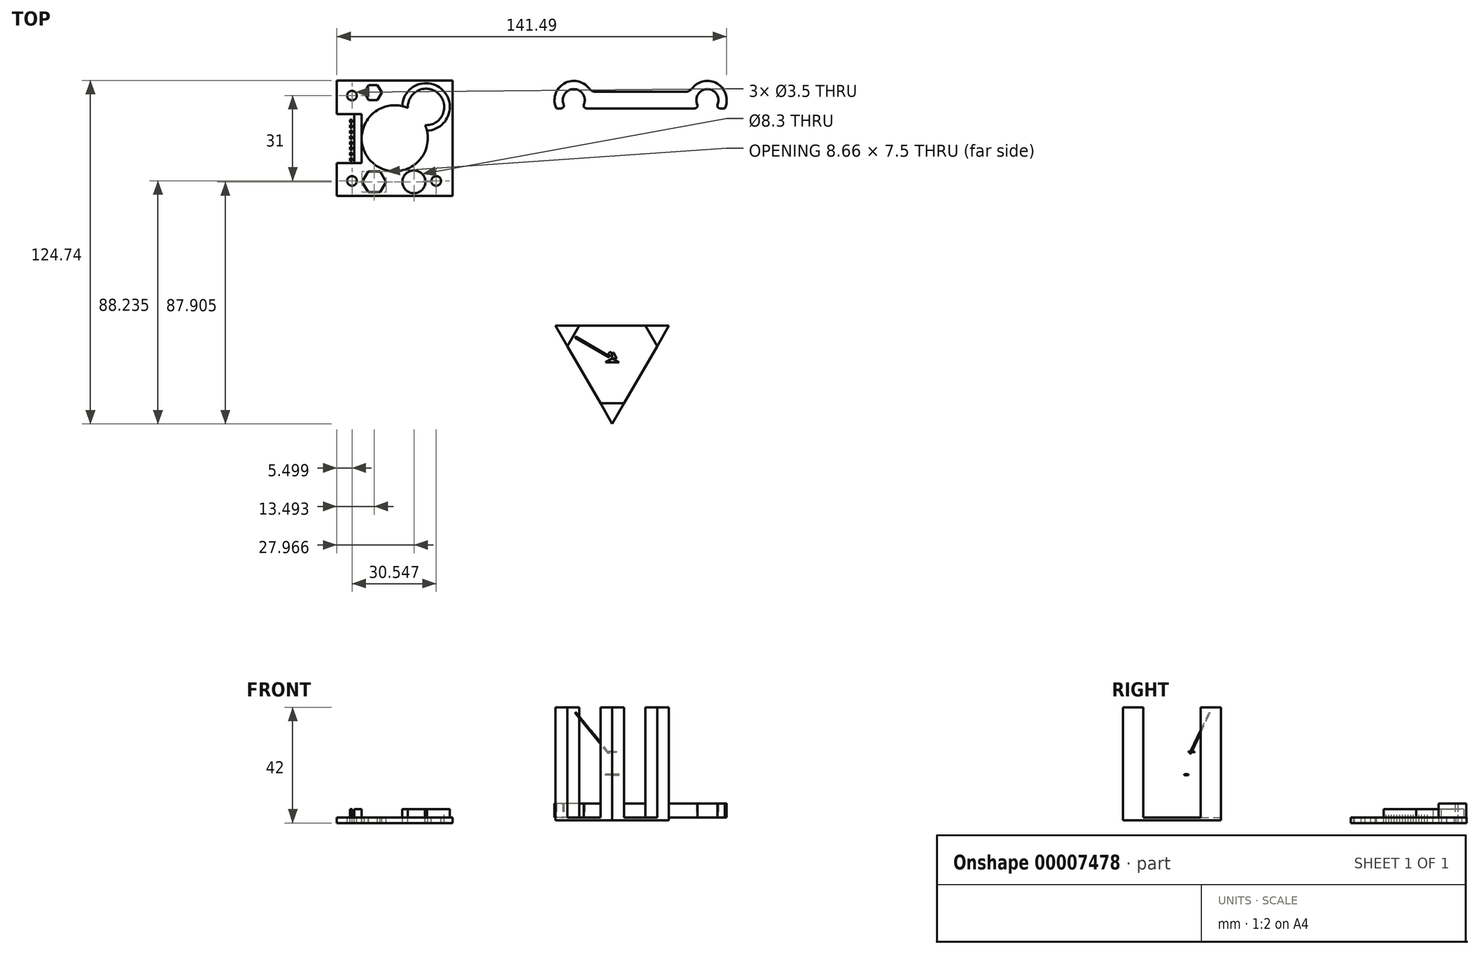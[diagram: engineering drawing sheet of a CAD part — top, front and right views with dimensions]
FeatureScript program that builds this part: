
annotation { "Feature Type Name" : "Feature", "Feature Type Description" : "" }
export const myFeature = defineFeature(function(context is Context, id is Id, definition is map)
    precondition{}
    {
        {
            var Q0;
            Q0=qCreatedBy(makeId("Top.planeOp"),FACE);
            var sketch = newSketch(context, id + "F0", { "sketchPlane" : qUnion([Q0])});
            skLineSegment(sketch, "E0.rect.bottom", {"start": v(36, -3) * mm, "end": v(-19.67, -3) * mm});
            skLineSegment(sketch, "E0.rect.top", {"start": v(36, 3) * mm, "end": v(-16.25, 3) * mm});
            skLineSegment(sketch, "E0.rect.left", {"start": v(36, -3) * mm, "end": v(36, 3) * mm});
            skPoint(sketch, "E0.rect.middle", {"position": v(0, 0) * mm});
            skArc(sketch, "E1", {"start": v(-18.65, 4.2) * mm, "mid": v(-27.87, 6) * mm, "end": v(-30.57, -3) * mm});
            skArc(sketch, "E2", {"start": v(-20.58, -1.6) * mm, "mid": v(-24.25, 4) * mm, "end": v(-27.92, -1.6) * mm});
            skLineSegment(sketch, "E3", {"start": v(-28.83, -3) * mm, "end": v(-30.57, -3) * mm});
            skPoint(sketch, "E0.rect.right.end.orphan", {"position": v(-36, 3) * mm});
            skLineSegment(sketch, "E4", {"start": v(0, 3) * mm, "end": v(0, -3) * mm});
            skPoint(sketch, "E5.orphan", {"position": v(-36, -3) * mm});
            skPoint(sketch, "E6.visualSharp", {"position": v(-26.9, -3) * mm});
            skArc(sketch, "E6.filletArc", {"start": v(-28.83, -3) * mm, "mid": v(-28, -2.55) * mm, "end": v(-27.92, -1.6) * mm});
            skPoint(sketch, "E7.visualSharp", {"position": v(-21.6, -3) * mm});
            skArc(sketch, "E7.filletArc", {"start": v(-20.58, -1.6) * mm, "mid": v(-20.5, -2.55) * mm, "end": v(-19.67, -3) * mm});
            skArc(sketch, "E8.filletArc", {"start": v(-18.65, 4.2) * mm, "mid": v(-17.6, 3.32) * mm, "end": v(-16.25, 3) * mm});
            skSolve(sketch);
        }
        {
            var Q0;
            Q0=makeQuery(id+"F0.imprint","IMPRINT",FACE,{"disambiguationData":[TD([[makeQuery(id+"F0.imprint","IMPRINT",EDGE,{"derivedFrom":sQuery(id+"F0.wireOp",EDGE,"E1")}),1.0]])]});
            extrude(context, id + "F1", {"entities" : qUnion([Q0]), "depth" : 5 * mm});
        }
        {
            var Q0;
            Q0=makeQuery(id+"F1.opExtrude","SWEPT_BODY",BODY,{"disambiguationData":[OSD([sQuery(id+"F0.wireOp",EDGE,"E0.rect.bottom"),sQuery(id+"F0.wireOp",EDGE,"E0.rect.top"),sQuery(id+"F0.wireOp",EDGE,"E1"),sQuery(id+"F0.wireOp",EDGE,"E2"),sQuery(id+"F0.wireOp",EDGE,"E3"),sQuery(id+"F0.wireOp",EDGE,"E4"),sQuery(id+"F0.wireOp",EDGE,"E6.filletArc"),sQuery(id+"F0.wireOp",EDGE,"E7.filletArc"),sQuery(id+"F0.wireOp",EDGE,"E8.filletArc")])]});
            var Q1;
            Q1=makeQuery(id+"F1.opExtrude","SWEPT_FACE",FACE,{"disambiguationData":[OSD([sQuery(id+"F0.wireOp",EDGE,"E4")])]});
            mirror(context, id + "F2", {"operationType" : NewBodyOperationType.ADD, "entities" : qUnion([Q0]), "mirrorPlane" : qUnion([Q1])});
        }
        {
            var Q0;
            Q0=qCreatedBy(makeId("Top.planeOp"),FACE);
            var sketch = newSketch(context, id + "F3", { "sketchPlane" : qUnion([Q0])});
            skCircle(sketch, "E9.cCircle", {"center": v(-10.28, -93.84) * mm, "radius": 11.87 * mm, "construction": true});
            skLineSegment(sketch, "E9.0", {"start": v(-30.84, -81.97) * mm, "end": v(10.29, -81.97) * mm});
            skLineSegment(sketch, "E9.1", {"start": v(10.29, -81.97) * mm, "end": v(-10.28, -117.59) * mm});
            skLineSegment(sketch, "E9.2", {"start": v(-10.28, -117.59) * mm, "end": v(-30.84, -81.97) * mm});
            skPoint(sketch, "E9.0.midPoint", {"position": v(-10.28, -81.97) * mm});
            skLineSegment(sketch, "E10", {"start": v(-22.28, -81.97) * mm, "end": v(-26.56, -89.39) * mm});
            skLineSegment(sketch, "E11.1.0", {"start": v(-14.56, -110.17) * mm, "end": v(-6, -110.17) * mm});
            skLineSegment(sketch, "E11.2.0", {"start": v(6, -89.39) * mm, "end": v(1.72, -81.97) * mm});
            skSolve(sketch);
        }
        {
            var Q0;
            {var subQ0=sQuery(id+"F3.wireOp",EDGE,"E10");Q0=makeQuery(id+"F3.imprint","IMPRINT",FACE,{"disambiguationData":[TD([[makeQuery(id+"F3.imprint","IMPRINT",EDGE,{"derivedFrom":subQ0}),-1.0]])]});}
            var Q1;
            {var subQ0=sQuery(id+"F3.wireOp",EDGE,"E11.1.0");Q1=makeQuery(id+"F3.imprint","IMPRINT",FACE,{"disambiguationData":[TD([[makeQuery(id+"F3.imprint","IMPRINT",EDGE,{"derivedFrom":subQ0}),-1.0]])]});}
            var Q2;
            {var subQ0=sQuery(id+"F3.wireOp",EDGE,"E11.2.0");Q2=makeQuery(id+"F3.imprint","IMPRINT",FACE,{"disambiguationData":[TD([[makeQuery(id+"F3.imprint","IMPRINT",EDGE,{"derivedFrom":subQ0}),-1.0]])]});}
            var Q3;
            {var subQ2=sQuery(id+"F3.wireOp",EDGE,"E10");Q3=makeQuery(id+"F3.imprint","IMPRINT",FACE,{"disambiguationData":[TD([[makeQuery(id+"F3.imprint","IMPRINT",EDGE,{"derivedFrom":subQ2}),1.0]])]});}
            extrude(context, id + "F4", {"entities" : qUnion([Q0, Q1, Q2, Q3]), "oppositeDirection" : true, "depth" : 1 * mm});
        }
        {
            var Q0;
            {var subQ0=sQuery(id+"F3.wireOp",EDGE,"E10");Q0=makeQuery(id+"F3.imprint","IMPRINT",FACE,{"disambiguationData":[TD([[makeQuery(id+"F3.imprint","IMPRINT",EDGE,{"derivedFrom":subQ0}),-1.0]])]});}
            var Q1;
            {var subQ0=sQuery(id+"F3.wireOp",EDGE,"E11.1.0");Q1=makeQuery(id+"F3.imprint","IMPRINT",FACE,{"disambiguationData":[TD([[makeQuery(id+"F3.imprint","IMPRINT",EDGE,{"derivedFrom":subQ0}),-1.0]])]});}
            var Q2;
            {var subQ0=sQuery(id+"F3.wireOp",EDGE,"E11.2.0");Q2=makeQuery(id+"F3.imprint","IMPRINT",FACE,{"disambiguationData":[TD([[makeQuery(id+"F3.imprint","IMPRINT",EDGE,{"derivedFrom":subQ0}),-1.0]])]});}
            extrude(context, id + "F5", {"entities" : qUnion([Q0, Q1, Q2]), "operationType" : NewBodyOperationType.ADD, "depth" : 40 * mm});
        }
        {
            var Q0;
            {var subQ2=sQuery(id+"F3.wireOp",EDGE,"E10");Q0=makeQuery(id+"F3.imprint","IMPRINT",FACE,{"disambiguationData":[TD([[makeQuery(id+"F3.imprint","IMPRINT",EDGE,{"derivedFrom":subQ2}),1.0]])]});}
            cPlane(context, id + "F6", {"entities" : qUnion([Q0]), "cplaneType" : CPlaneType.OFFSET, "offset" : 24 * mm, "width" : 150 * mm, "height" : 150 * mm});
        }
        {
            var Q0;
            Q0=qCreatedBy(id+"F6.planeOp",FACE);
            var sketch = newSketch(context, id + "F7", { "sketchPlane" : qUnion([Q0])});
            skLineSegment(sketch, "E12", {"start": v(-11.53, -93.12) * mm, "end": v(-24.42, -85.68) * mm});
            skLineSegment(sketch, "E13.0", {"start": v(-22.28, -81.97) * mm, "end": v(-26.56, -89.39) * mm});
            skPoint(sketch, "E14.0", {"position": v(-10.28, -93.84) * mm});
            skLineSegment(sketch, "E15", {"start": v(-10.28, -93.84) * mm, "end": v(-12.78, -95.29) * mm});
            skLineSegment(sketch, "E16", {"start": v(-12.78, -95.29) * mm, "end": v(-10.28, -90.96) * mm});
            skLineSegment(sketch, "E17", {"start": v(-10.28, -90.96) * mm, "end": v(-10.28, -93.84) * mm});
            skLineSegment(sketch, "E18", {"start": v(-10.28, -93.84) * mm, "end": v(-6.88, -93.84) * mm});
            skLineSegment(sketch, "E19", {"start": v(-11, -92.21) * mm, "end": v(-12.05, -94.03) * mm});
            skLineSegment(sketch, "E20.1.0", {"start": v(-7.78, -95.29) * mm, "end": v(-12.78, -95.29) * mm});
            skLineSegment(sketch, "E20.1.1", {"start": v(-12.78, -95.29) * mm, "end": v(-10.28, -93.84) * mm});
            skLineSegment(sketch, "E20.1.2", {"start": v(-10.28, -93.84) * mm, "end": v(-7.78, -95.29) * mm});
            skLineSegment(sketch, "E20.2.0", {"start": v(-10.28, -90.96) * mm, "end": v(-7.78, -95.29) * mm});
            skLineSegment(sketch, "E20.2.1", {"start": v(-7.78, -95.29) * mm, "end": v(-10.28, -93.84) * mm});
            skLineSegment(sketch, "E20.2.2", {"start": v(-10.28, -93.84) * mm, "end": v(-10.28, -90.96) * mm});
            skLineSegment(sketch, "E21", {"start": v(-11, -92.21) * mm, "end": v(-9.55, -92.21) * mm});
            skCircle(sketch, "E22", {"center": v(-11, -92.21) * mm, "radius": 0.6 * mm});
            skCircle(sketch, "E23", {"center": v(-9.55, -92.21) * mm, "radius": 0.6 * mm});
            skSolve(sketch);
        }
        {
            var Q0;
            Q0=sQuery(id+"F7.wireOp",EDGE,"E12");
            var Q1;
            Q1=makeQuery(id+"F5.opExtrude","CAP_FACE",FACE,{"disambiguationData":[OSD([sQuery(id+"F3.wireOp",EDGE,"E9.0"),sQuery(id+"F3.wireOp",EDGE,"E9.2"),sQuery(id+"F3.wireOp",EDGE,"E10")])],"isStart":false});
            extrude(context, id + "F8", {"bodyType" : ToolBodyType.SURFACE, "surfaceEntities" : qUnion([Q0]), "endBound" : BoundingType.UP_TO_SURFACE, "endBoundEntityFace" : qUnion([Q1]), "depth" : 25 * mm});
        }
        {
            var Q0;
            Q0=makeQuery(id+"F8.opExtrude","SWEPT_FACE",FACE,{"disambiguationData":[OSD([sQuery(id+"F7.wireOp",EDGE,"E12")])]});
            var sketch = newSketch(context, id + "F9", { "sketchPlane" : qUnion([Q0])});
            skLineSegment(sketch, "E24", {"start": v(-22.7, 38) * mm, "end": v(-36.58, 23.33) * mm});
            skLineSegment(sketch, "E25", {"start": v(-36.58, 23.33) * mm, "end": v(-22.7, 23.33) * mm});
            skLineSegment(sketch, "E26", {"start": v(-22.7, 23.33) * mm, "end": v(-22.7, 38) * mm});
            skLineSegment(sketch, "E27", {"start": v(-22.7, 38) * mm, "end": v(-21.7, 38) * mm});
            skLineSegment(sketch, "E28", {"start": v(-22.7, 38) * mm, "end": v(-24.45, 17.88) * mm});
            skLineSegment(sketch, "E29", {"start": v(-24.45, 17.88) * mm, "end": v(-22.7, 17.88) * mm});
            skLineSegment(sketch, "E30", {"start": v(-22.7, 17.88) * mm, "end": v(-22.7, 23.33) * mm});
            skPoint(sketch, "E31.0", {"position": v(-21.7, 0) * mm});
            skCircle(sketch, "E32", {"center": v(-22.7, 38) * mm, "radius": 20.2 * mm, "construction": true});
            skLineSegment(sketch, "E33.0", {"start": v(-22.84, 38.14) * mm, "end": v(-36.72, 23.47) * mm});
            skLineSegment(sketch, "E34", {"start": v(-36.72, 23.47) * mm, "end": v(-36.58, 23.33) * mm});
            skLineSegment(sketch, "E35", {"start": v(-22.7, 38) * mm, "end": v(-22.84, 38.14) * mm});
            skLineSegment(sketch, "E36", {"start": v(-36.58, 23.33) * mm, "end": v(-36.58, 19.83) * mm});
            skLineSegment(sketch, "E37", {"start": v(-24.45, 17.88) * mm, "end": v(-24.45, 14.38) * mm});
            skLineSegment(sketch, "E38.0", {"start": v(-42.47, 40) * mm, "end": v(-42.47, 0) * mm});
            skSolve(sketch);
        }
        {
            var Q0;
            {var subQ0=sQuery(id+"F7.wireOp",EDGE,"E22");var subQ3=sQuery(id+"F7.wireOp",EDGE,"E16");var subQ4=makeQuery(id+"F7.imprint","INTERSECT",VERTEX,{"derivedFrom":[subQ3,subQ0]});Q0=makeQuery(id+"F7.imprint","IMPRINT",FACE,{"disambiguationData":[TD([[makeQuery(id+"F7.imprint","IMPRINT",EDGE,{"disambiguationData":[TD([[subQ4,1.0]])],"derivedFrom":subQ0}),1.0]])]});}
            var Q1;
            {var subQ0=sQuery(id+"F7.wireOp",EDGE,"E22");var subQ3=sQuery(id+"F7.wireOp",EDGE,"E19");var subQ4=makeQuery(id+"F7.imprint","INTERSECT",VERTEX,{"derivedFrom":[subQ3,subQ0]});Q1=makeQuery(id+"F7.imprint","IMPRINT",FACE,{"disambiguationData":[TD([[makeQuery(id+"F7.imprint","IMPRINT",EDGE,{"disambiguationData":[TD([[subQ4,-1.0]])],"derivedFrom":subQ0}),1.0]])]});}
            var Q2;
            {var subQ3=sQuery(id+"F7.wireOp",EDGE,"E20.1.1");Q2=makeQuery(id+"F7.imprint","IMPRINT",FACE,{"disambiguationData":[TD([[makeQuery(id+"F7.imprint","IMPRINT",EDGE,{"derivedFrom":subQ3}),1.0]])]});}
            var Q3;
            {var subQ1=sQuery(id+"F7.wireOp",EDGE,"E21");var subQ5=sQuery(id+"F7.wireOp",EDGE,"E20.2.2");var subQ6=makeQuery(id+"F7.imprint","INTERSECT",VERTEX,{"derivedFrom":[subQ5,subQ1]});Q3=makeQuery(id+"F7.imprint","IMPRINT",FACE,{"disambiguationData":[TD([[makeQuery(id+"F7.imprint","IMPRINT",EDGE,{"disambiguationData":[TD([[subQ6,1.0]])],"derivedFrom":subQ1}),1.0]])]});}
            var Q4;
            {var subQ1=sQuery(id+"F7.wireOp",EDGE,"E21");var subQ5=sQuery(id+"F7.wireOp",EDGE,"E20.2.2");var subQ6=makeQuery(id+"F7.imprint","INTERSECT",VERTEX,{"derivedFrom":[subQ5,subQ1]});Q4=makeQuery(id+"F7.imprint","IMPRINT",FACE,{"disambiguationData":[TD([[makeQuery(id+"F7.imprint","IMPRINT",EDGE,{"disambiguationData":[TD([[subQ6,-1.0]])],"derivedFrom":subQ1}),1.0]])]});}
            var Q5;
            {var subQ1=sQuery(id+"F7.wireOp",EDGE,"E21");var subQ3=sQuery(id+"F7.wireOp",EDGE,"E20.2.0");var subQ5=makeQuery(id+"F7.imprint","INTERSECT",VERTEX,{"derivedFrom":[subQ3,subQ1]});Q5=makeQuery(id+"F7.imprint","IMPRINT",FACE,{"disambiguationData":[TD([[makeQuery(id+"F7.imprint","IMPRINT",EDGE,{"disambiguationData":[TD([[subQ5,1.0]])],"derivedFrom":subQ3}),-1.0]])]});}
            var Q6;
            {var subQ1=sQuery(id+"F7.wireOp",EDGE,"E21");var subQ3=sQuery(id+"F7.wireOp",EDGE,"E20.2.0");var subQ5=makeQuery(id+"F7.imprint","INTERSECT",VERTEX,{"derivedFrom":[subQ3,subQ1]});Q6=makeQuery(id+"F7.imprint","IMPRINT",FACE,{"disambiguationData":[TD([[makeQuery(id+"F7.imprint","IMPRINT",EDGE,{"disambiguationData":[TD([[subQ5,-1.0]])],"derivedFrom":subQ3}),-1.0]])]});}
            var Q7;
            {var subQ3=sQuery(id+"F7.wireOp",EDGE,"E20.2.0");var subQ7=sQuery(id+"F7.wireOp",EDGE,"E18");var subQ9=makeQuery(id+"F7.imprint","INTERSECT",VERTEX,{"derivedFrom":[subQ7,subQ3]});Q7=makeQuery(id+"F7.imprint","IMPRINT",FACE,{"disambiguationData":[TD([[makeQuery(id+"F7.imprint","IMPRINT",EDGE,{"disambiguationData":[TD([[subQ9,1.0]])],"derivedFrom":subQ3}),-1.0]])]});}
            var Q8;
            {var subQ0=sQuery(id+"F7.wireOp",EDGE,"E20.2.1");Q8=makeQuery(id+"F7.imprint","IMPRINT",FACE,{"disambiguationData":[TD([[makeQuery(id+"F7.imprint","IMPRINT",EDGE,{"derivedFrom":subQ0}),-1.0]])]});}
            var Q9;
            Q9=makeQuery(id+"F7.imprint","IMPRINT",FACE,{"disambiguationData":[TD([[makeQuery(id+"F7.imprint","IMPRINT",EDGE,{"derivedFrom":sQuery(id+"F7.wireOp",EDGE,"E20.1.0")}),-1.0]])]});
            extrude(context, id + "F10", {"entities" : qUnion([Q0, Q1, Q2, Q3, Q4, Q5, Q6, Q7, Q8, Q9]), "oppositeDirection" : true, "depth" : 0.3 * mm});
        }
        {
            var Q0;
            Q0=makeQuery(id+"F10.opExtrude","SWEPT_BODY",BODY,{"disambiguationData":[OSD([sQuery(id+"F7.wireOp",EDGE,"E16"),sQuery(id+"F7.wireOp",EDGE,"E19"),sQuery(id+"F7.wireOp",EDGE,"E20.1.0"),sQuery(id+"F7.wireOp",EDGE,"E20.2.0")])]});
            var Q1;
            Q1=sQuery(id+"F9.wireOp",EDGE,"E26");
            transform(context, id + "F11", {"entities" : qUnion([Q0]), "transformType" : TransformType.TRANSLATION_3D, "dx" : 0 * mm, "dy" : 0 * mm, "dz" : -8.29 * mm, "makeCopy" : false});
        }
        {
            var Q0;
            {var subQ5=sQuery(id+"F9.wireOp",EDGE,"E35");Q0=makeQuery(id+"F9.imprint","IMPRINT",FACE,{"disambiguationData":[TD([[makeQuery(id+"F9.imprint","IMPRINT",EDGE,{"derivedFrom":subQ5}),1.0]])]});}
            var Q1;
            {var subQ0=sQuery(id+"F9.wireOp",EDGE,"E34");Q1=makeQuery(id+"F9.imprint","IMPRINT",FACE,{"disambiguationData":[TD([[makeQuery(id+"F9.imprint","IMPRINT",EDGE,{"derivedFrom":subQ0}),1.0]])]});}
            var Q2;
            Q2=sQuery(id+"F9.wireOp",EDGE,"E24");
            revolve(context, id + "F12", {"entities" : qUnion([Q0, Q1]), "axis" : qUnion([Q2]), "revolveType" : RevolveType.FULL});
        }
        {
            var Q0;
            Q0=qCreatedBy(makeId("Top.planeOp"),FACE);
            var sketch = newSketch(context, id + "F13", { "sketchPlane" : qUnion([Q0])});
            skLineSegment(sketch, "E39.rect.bottom", {"start": v(-68.24, -34.85) * mm, "end": v(-110.24, -34.85) * mm});
            skLineSegment(sketch, "E39.rect.top", {"start": v(-68.24, 7.15) * mm, "end": v(-110.24, 7.15) * mm});
            skLineSegment(sketch, "E39.rect.left", {"start": v(-68.24, -34.85) * mm, "end": v(-68.24, 7.15) * mm});
            skLineSegment(sketch, "E39.rect.right", {"start": v(-110.24, -34.85) * mm, "end": v(-110.24, 7.15) * mm});
            skPoint(sketch, "E39.rect.middle", {"position": v(-89.24, -13.85) * mm});
            skCircle(sketch, "E40", {"center": v(-77.87, -2.49) * mm, "radius": 6.62 * mm});
            skLineSegment(sketch, "E41", {"start": v(-77.87, -2.49) * mm, "end": v(-68.24, 7.15) * mm});
            skCircle(sketch, "E42", {"center": v(-89.24, -13.85) * mm, "radius": 12 * mm});
            skLineSegment(sketch, "E43.0", {"start": v(-68.24, -29.35) * mm, "end": v(-104.74, -29.35) * mm, "construction": true});
            skLineSegment(sketch, "E43.1", {"start": v(-104.74, -29.35) * mm, "end": v(-104.74, 1.65) * mm, "construction": true});
            skLineSegment(sketch, "E43.2", {"start": v(-68.24, 1.65) * mm, "end": v(-104.74, 1.65) * mm, "construction": true});
            skCircle(sketch, "E44", {"center": v(-104.74, 1.65) * mm, "radius": 1.75 * mm});
            skCircle(sketch, "E45", {"center": v(-104.74, -29.35) * mm, "radius": 1.75 * mm});
            skCircle(sketch, "E46", {"center": v(-74.2, -29.35) * mm, "radius": 1.75 * mm});
            skLineSegment(sketch, "E47.bottom", {"start": v(-110.24, -22.88) * mm, "end": v(-101.24, -22.88) * mm});
            skLineSegment(sketch, "E47.top", {"start": v(-110.24, -5.08) * mm, "end": v(-101.24, -5.08) * mm});
            skLineSegment(sketch, "E47.left", {"start": v(-110.24, -22.88) * mm, "end": v(-110.24, -5.08) * mm});
            skLineSegment(sketch, "E47.right", {"start": v(-101.24, -22.88) * mm, "end": v(-101.24, -5.08) * mm});
            skLineSegment(sketch, "E48", {"start": v(-110.24, -13.98) * mm, "end": v(-104.74, -13.98) * mm, "construction": true});
            skLineSegment(sketch, "E49.rect.bottom", {"start": v(-104, -22.88) * mm, "end": v(-105.5, -22.88) * mm});
            skLineSegment(sketch, "E49.rect.top", {"start": v(-104, -5.08) * mm, "end": v(-105.5, -5.08) * mm});
            skLineSegment(sketch, "E49.rect.left", {"start": v(-104, -22.88) * mm, "end": v(-104, -5.08) * mm});
            skLineSegment(sketch, "E49.rect.right", {"start": v(-105.5, -22.88) * mm, "end": v(-105.5, -5.08) * mm});
            skPoint(sketch, "E49.rect.middle", {"position": v(-104.74, -13.98) * mm});
            skLineSegment(sketch, "E50.bottom", {"start": v(-105.5, -5.08) * mm, "end": v(-104.7, -5.08) * mm});
            skLineSegment(sketch, "E50.top", {"start": v(-105.5, -6.08) * mm, "end": v(-104.7, -6.08) * mm});
            skLineSegment(sketch, "E50.left", {"start": v(-105.5, -5.08) * mm, "end": v(-105.5, -6.08) * mm});
            skLineSegment(sketch, "E50.right", {"start": v(-104.7, -5.08) * mm, "end": v(-104.7, -6.08) * mm});
            skLineSegment(sketch, "E51.0.1.0", {"start": v(-105.5, -8.08) * mm, "end": v(-104.7, -8.08) * mm});
            skLineSegment(sketch, "E51.0.1.1", {"start": v(-104.7, -7.08) * mm, "end": v(-104.7, -8.08) * mm});
            skLineSegment(sketch, "E51.0.1.2", {"start": v(-105.5, -7.08) * mm, "end": v(-104.7, -7.08) * mm});
            skLineSegment(sketch, "E51.0.2.0", {"start": v(-105.5, -10.08) * mm, "end": v(-104.7, -10.08) * mm});
            skLineSegment(sketch, "E51.0.2.1", {"start": v(-104.7, -9.08) * mm, "end": v(-104.7, -10.08) * mm});
            skLineSegment(sketch, "E51.0.2.2", {"start": v(-105.5, -9.08) * mm, "end": v(-104.7, -9.08) * mm});
            skLineSegment(sketch, "E51.0.3.0", {"start": v(-105.5, -12.08) * mm, "end": v(-104.7, -12.08) * mm});
            skLineSegment(sketch, "E51.0.3.1", {"start": v(-104.7, -11.08) * mm, "end": v(-104.7, -12.08) * mm});
            skLineSegment(sketch, "E51.0.3.2", {"start": v(-105.5, -11.08) * mm, "end": v(-104.7, -11.08) * mm});
            skLineSegment(sketch, "E51.0.4.0", {"start": v(-105.5, -14.08) * mm, "end": v(-104.7, -14.08) * mm});
            skLineSegment(sketch, "E51.0.4.1", {"start": v(-104.7, -13.08) * mm, "end": v(-104.7, -14.08) * mm});
            skLineSegment(sketch, "E51.0.4.2", {"start": v(-105.5, -13.08) * mm, "end": v(-104.7, -13.08) * mm});
            skLineSegment(sketch, "E51.0.5.0", {"start": v(-105.5, -16.08) * mm, "end": v(-104.7, -16.08) * mm});
            skLineSegment(sketch, "E51.0.5.1", {"start": v(-104.7, -15.08) * mm, "end": v(-104.7, -16.08) * mm});
            skLineSegment(sketch, "E51.0.5.2", {"start": v(-105.5, -15.08) * mm, "end": v(-104.7, -15.08) * mm});
            skLineSegment(sketch, "E51.0.6.0", {"start": v(-105.5, -18.08) * mm, "end": v(-104.7, -18.08) * mm});
            skLineSegment(sketch, "E51.0.6.1", {"start": v(-104.7, -17.08) * mm, "end": v(-104.7, -18.08) * mm});
            skLineSegment(sketch, "E51.0.6.2", {"start": v(-105.5, -17.08) * mm, "end": v(-104.7, -17.08) * mm});
            skLineSegment(sketch, "E51.0.7.0", {"start": v(-105.5, -20.08) * mm, "end": v(-104.7, -20.08) * mm});
            skLineSegment(sketch, "E51.0.7.1", {"start": v(-104.7, -19.08) * mm, "end": v(-104.7, -20.08) * mm});
            skLineSegment(sketch, "E51.0.7.2", {"start": v(-105.5, -19.08) * mm, "end": v(-104.7, -19.08) * mm});
            skLineSegment(sketch, "E51.0.8.0", {"start": v(-105.5, -22.08) * mm, "end": v(-104.7, -22.08) * mm});
            skLineSegment(sketch, "E51.0.8.1", {"start": v(-104.7, -21.08) * mm, "end": v(-104.7, -22.08) * mm});
            skLineSegment(sketch, "E51.0.8.2", {"start": v(-105.5, -21.08) * mm, "end": v(-104.7, -21.08) * mm});
            skLineSegment(sketch, "E51.0.9.0", {"start": v(-105.5, -24.08) * mm, "end": v(-104.7, -24.08) * mm});
            skLineSegment(sketch, "E51.0.9.1", {"start": v(-104.7, -23.08) * mm, "end": v(-104.7, -24.08) * mm});
            skLineSegment(sketch, "E51.0.9.2", {"start": v(-105.5, -23.08) * mm, "end": v(-104.7, -23.08) * mm});
            skLineSegment(sketch, "E51.direction1", {"start": v(-105.5, -6.08) * mm, "end": v(-80.5, -6.08) * mm, "construction": true});
            skLineSegment(sketch, "E51.direction2", {"start": v(-105.5, -6.08) * mm, "end": v(-105.5, -8.08) * mm, "construction": true});
            skSolve(sketch);
        }
        {
            var Q0;
            {var subQ13=sQuery(id+"F13.wireOp",EDGE,"E39.rect.top");Q0=makeQuery(id+"F13.imprint","IMPRINT",FACE,{"disambiguationData":[TD([[makeQuery(id+"F13.imprint","IMPRINT",EDGE,{"derivedFrom":subQ13}),1.0]])]});}
            var Q1;
            {var subQ13=sQuery(id+"F13.wireOp",EDGE,"E39.rect.bottom");Q1=makeQuery(id+"F13.imprint","IMPRINT",FACE,{"disambiguationData":[TD([[makeQuery(id+"F13.imprint","IMPRINT",EDGE,{"derivedFrom":subQ13}),-1.0]])]});}
            var Q2;
            {var subQ20=sQuery(id+"F13.wireOp",EDGE,"E47.left");Q2=makeQuery(id+"F13.imprint","IMPRINT",FACE,{"disambiguationData":[TD([[makeQuery(id+"F13.imprint","IMPRINT",EDGE,{"derivedFrom":subQ20}),-1.0]])]});}
            var Q3;
            {var subQ0=sQuery(id+"F13.wireOp",EDGE,"E49.rect.left");Q3=makeQuery(id+"F13.imprint","IMPRINT",FACE,{"disambiguationData":[TD([[makeQuery(id+"F13.imprint","IMPRINT",EDGE,{"derivedFrom":subQ0}),-1.0]])]});}
            var Q4;
            {var subQ7=sQuery(id+"F13.wireOp",EDGE,"E49.rect.bottom");Q4=makeQuery(id+"F13.imprint","IMPRINT",FACE,{"disambiguationData":[TD([[makeQuery(id+"F13.imprint","IMPRINT",EDGE,{"derivedFrom":subQ7}),-1.0]])]});}
            var Q5;
            Q5=makeQuery(id+"F13.imprint","IMPRINT",FACE,{"disambiguationData":[TD([[makeQuery(id+"F13.imprint","IMPRINT",EDGE,{"derivedFrom":sQuery(id+"F13.wireOp",EDGE,"E50.bottom")}),-1.0]])]});
            var Q6;
            {var subQ1=sQuery(id+"F13.wireOp",EDGE,"E51.0.8.0");Q6=makeQuery(id+"F13.imprint","IMPRINT",FACE,{"disambiguationData":[TD([[makeQuery(id+"F13.imprint","IMPRINT",EDGE,{"derivedFrom":subQ1}),1.0]])]});}
            var Q7;
            {var subQ1=sQuery(id+"F13.wireOp",EDGE,"E51.0.7.0");Q7=makeQuery(id+"F13.imprint","IMPRINT",FACE,{"disambiguationData":[TD([[makeQuery(id+"F13.imprint","IMPRINT",EDGE,{"derivedFrom":subQ1}),1.0]])]});}
            var Q8;
            {var subQ1=sQuery(id+"F13.wireOp",EDGE,"E51.0.6.0");Q8=makeQuery(id+"F13.imprint","IMPRINT",FACE,{"disambiguationData":[TD([[makeQuery(id+"F13.imprint","IMPRINT",EDGE,{"derivedFrom":subQ1}),1.0]])]});}
            var Q9;
            {var subQ1=sQuery(id+"F13.wireOp",EDGE,"E51.0.5.0");Q9=makeQuery(id+"F13.imprint","IMPRINT",FACE,{"disambiguationData":[TD([[makeQuery(id+"F13.imprint","IMPRINT",EDGE,{"derivedFrom":subQ1}),1.0]])]});}
            var Q10;
            {var subQ0=sQuery(id+"F13.wireOp",EDGE,"E51.0.3.0");Q10=makeQuery(id+"F13.imprint","IMPRINT",FACE,{"disambiguationData":[TD([[makeQuery(id+"F13.imprint","IMPRINT",EDGE,{"derivedFrom":subQ0}),1.0]])]});}
            var Q11;
            {var subQ1=sQuery(id+"F13.wireOp",EDGE,"E51.0.2.0");Q11=makeQuery(id+"F13.imprint","IMPRINT",FACE,{"disambiguationData":[TD([[makeQuery(id+"F13.imprint","IMPRINT",EDGE,{"derivedFrom":subQ1}),1.0]])]});}
            var Q12;
            {var subQ1=sQuery(id+"F13.wireOp",EDGE,"E51.0.1.0");Q12=makeQuery(id+"F13.imprint","IMPRINT",FACE,{"disambiguationData":[TD([[makeQuery(id+"F13.imprint","IMPRINT",EDGE,{"derivedFrom":subQ1}),1.0]])]});}
            var Q13;
            {var subQ1=sQuery(id+"F13.wireOp",EDGE,"E51.0.4.0");Q13=makeQuery(id+"F13.imprint","IMPRINT",FACE,{"disambiguationData":[TD([[makeQuery(id+"F13.imprint","IMPRINT",EDGE,{"derivedFrom":subQ1}),1.0]])]});}
            extrude(context, id + "F14", {"entities" : qUnion([Q0, Q1, Q2, Q3, Q4, Q5, Q6, Q7, Q8, Q9, Q10, Q11, Q12, Q13]), "oppositeDirection" : true, "depth" : 2 * mm});
        }
        {
            var Q0;
            {var subQ20=sQuery(id+"F13.wireOp",EDGE,"E47.left");Q0=makeQuery(id+"F13.imprint","IMPRINT",FACE,{"disambiguationData":[TD([[makeQuery(id+"F13.imprint","IMPRINT",EDGE,{"derivedFrom":subQ20}),-1.0]])]});}
            var Q1;
            Q1=makeQuery(id+"F13.imprint","IMPRINT",FACE,{"disambiguationData":[TD([[makeQuery(id+"F13.imprint","IMPRINT",EDGE,{"derivedFrom":sQuery(id+"F13.wireOp",EDGE,"E50.bottom")}),-1.0]])]});
            var Q2;
            {var subQ1=sQuery(id+"F13.wireOp",EDGE,"E51.0.1.0");Q2=makeQuery(id+"F13.imprint","IMPRINT",FACE,{"disambiguationData":[TD([[makeQuery(id+"F13.imprint","IMPRINT",EDGE,{"derivedFrom":subQ1}),1.0]])]});}
            var Q3;
            {var subQ1=sQuery(id+"F13.wireOp",EDGE,"E51.0.2.0");Q3=makeQuery(id+"F13.imprint","IMPRINT",FACE,{"disambiguationData":[TD([[makeQuery(id+"F13.imprint","IMPRINT",EDGE,{"derivedFrom":subQ1}),1.0]])]});}
            var Q4;
            {var subQ0=sQuery(id+"F13.wireOp",EDGE,"E51.0.3.0");Q4=makeQuery(id+"F13.imprint","IMPRINT",FACE,{"disambiguationData":[TD([[makeQuery(id+"F13.imprint","IMPRINT",EDGE,{"derivedFrom":subQ0}),1.0]])]});}
            var Q5;
            {var subQ1=sQuery(id+"F13.wireOp",EDGE,"E51.0.4.0");Q5=makeQuery(id+"F13.imprint","IMPRINT",FACE,{"disambiguationData":[TD([[makeQuery(id+"F13.imprint","IMPRINT",EDGE,{"derivedFrom":subQ1}),1.0]])]});}
            var Q6;
            {var subQ1=sQuery(id+"F13.wireOp",EDGE,"E51.0.5.0");Q6=makeQuery(id+"F13.imprint","IMPRINT",FACE,{"disambiguationData":[TD([[makeQuery(id+"F13.imprint","IMPRINT",EDGE,{"derivedFrom":subQ1}),1.0]])]});}
            var Q7;
            {var subQ1=sQuery(id+"F13.wireOp",EDGE,"E51.0.6.0");Q7=makeQuery(id+"F13.imprint","IMPRINT",FACE,{"disambiguationData":[TD([[makeQuery(id+"F13.imprint","IMPRINT",EDGE,{"derivedFrom":subQ1}),1.0]])]});}
            var Q8;
            {var subQ1=sQuery(id+"F13.wireOp",EDGE,"E51.0.7.0");Q8=makeQuery(id+"F13.imprint","IMPRINT",FACE,{"disambiguationData":[TD([[makeQuery(id+"F13.imprint","IMPRINT",EDGE,{"derivedFrom":subQ1}),1.0]])]});}
            var Q9;
            {var subQ0=sQuery(id+"F13.wireOp",EDGE,"E49.rect.left");Q9=makeQuery(id+"F13.imprint","IMPRINT",FACE,{"disambiguationData":[TD([[makeQuery(id+"F13.imprint","IMPRINT",EDGE,{"derivedFrom":subQ0}),-1.0]])]});}
            var Q10;
            {var subQ1=sQuery(id+"F13.wireOp",EDGE,"E51.0.8.0");Q10=makeQuery(id+"F13.imprint","IMPRINT",FACE,{"disambiguationData":[TD([[makeQuery(id+"F13.imprint","IMPRINT",EDGE,{"derivedFrom":subQ1}),1.0]])]});}
            extrude(context, id + "F15", {"entities" : qUnion([Q0, Q1, Q2, Q3, Q4, Q5, Q6, Q7, Q8, Q9, Q10]), "operationType" : NewBodyOperationType.ADD, "depth" : 3 * mm});
        }
        {
            var Q0;
            {var subQ13=sQuery(id+"F13.wireOp",EDGE,"E39.rect.top");Q0=makeQuery(id+"F13.imprint","IMPRINT",FACE,{"disambiguationData":[TD([[makeQuery(id+"F13.imprint","IMPRINT",EDGE,{"derivedFrom":subQ13}),1.0]])]});}
            var sketch = newSketch(context, id + "F16", { "sketchPlane" : qUnion([Q0])});
            skCircle(sketch, "E52.0", {"center": v(-77.87, -2.49) * mm, "radius": 6.62 * mm});
            skCircle(sketch, "E53", {"center": v(-77.87, -2.49) * mm, "radius": 8.62 * mm});
            skCircle(sketch, "E54.0", {"center": v(-89.24, -13.85) * mm, "radius": 12 * mm});
            skCircle(sketch, "E55.cCircle", {"center": v(-97.11, 2.75) * mm, "radius": 2.75 * mm, "construction": true});
            skLineSegment(sketch, "E55.0", {"start": v(-95.53, 0) * mm, "end": v(-98.7, 0) * mm});
            skLineSegment(sketch, "E55.1", {"start": v(-98.7, 0) * mm, "end": v(-100.3, 2.75) * mm});
            skLineSegment(sketch, "E55.2", {"start": v(-100.3, 2.75) * mm, "end": v(-98.7, 5.5) * mm});
            skLineSegment(sketch, "E55.3", {"start": v(-98.7, 5.5) * mm, "end": v(-95.53, 5.5) * mm});
            skLineSegment(sketch, "E55.4", {"start": v(-95.53, 5.5) * mm, "end": v(-93.94, 2.75) * mm});
            skLineSegment(sketch, "E55.5", {"start": v(-93.94, 2.75) * mm, "end": v(-95.53, 0) * mm});
            skPoint(sketch, "E55.0.midPoint", {"position": v(-97.11, 0) * mm});
            skCircle(sketch, "E56.cCircle", {"center": v(-96.75, -29.69) * mm, "radius": 3.75 * mm, "construction": true});
            skLineSegment(sketch, "E56.0", {"start": v(-94.58, -33.44) * mm, "end": v(-98.91, -33.44) * mm});
            skLineSegment(sketch, "E56.1", {"start": v(-98.91, -33.44) * mm, "end": v(-101.08, -29.69) * mm});
            skLineSegment(sketch, "E56.2", {"start": v(-101.08, -29.69) * mm, "end": v(-98.91, -25.94) * mm});
            skLineSegment(sketch, "E56.3", {"start": v(-98.91, -25.94) * mm, "end": v(-94.58, -25.94) * mm});
            skLineSegment(sketch, "E56.4", {"start": v(-94.58, -25.94) * mm, "end": v(-92.42, -29.69) * mm});
            skLineSegment(sketch, "E56.5", {"start": v(-92.42, -29.69) * mm, "end": v(-94.58, -33.44) * mm});
            skPoint(sketch, "E56.0.midPoint", {"position": v(-96.75, -33.44) * mm});
            skCircle(sketch, "E57", {"center": v(-82.27, -29.69) * mm, "radius": 4.15 * mm});
            skSolve(sketch);
        }
        {
            var Q0;
            {var subQ2=sQuery(id+"F16.wireOp",EDGE,"E53");var subQ6=sQuery(id+"F16.wireOp",EDGE,"E54.0");var subQ8=makeQuery(id+"F16.imprint","INTERSECT",VERTEX,{"disambiguationData":[OD(0.0)],"derivedFrom":[subQ2,subQ6]});Q0=makeQuery(id+"F16.imprint","IMPRINT",FACE,{"disambiguationData":[TD([[makeQuery(id+"F16.imprint","IMPRINT",EDGE,{"disambiguationData":[TD([[subQ8,-1.0]])],"derivedFrom":subQ6}),-1.0]])]});}
            var Q1;
            {var subQ4=sQuery(id+"F16.wireOp",EDGE,"E52.0");var subQ6=sQuery(id+"F16.wireOp",EDGE,"E54.0");var subQ8=makeQuery(id+"F16.imprint","INTERSECT",VERTEX,{"disambiguationData":[OD(0.0)],"derivedFrom":[subQ4,subQ6]});Q1=makeQuery(id+"F16.imprint","IMPRINT",FACE,{"disambiguationData":[TD([[makeQuery(id+"F16.imprint","IMPRINT",EDGE,{"disambiguationData":[TD([[subQ8,-1.0]])],"derivedFrom":subQ6}),-1.0]])]});}
            extrude(context, id + "F17", {"entities" : qUnion([Q0, Q1]), "operationType" : NewBodyOperationType.ADD, "depth" : 3 * mm});
        }
        {
            var Q0;
            Q0=makeQuery(id+"F16.imprint","IMPRINT",FACE,{"disambiguationData":[TD([[makeQuery(id+"F16.imprint","IMPRINT",EDGE,{"derivedFrom":sQuery(id+"F16.wireOp",EDGE,"E55.0")}),-1.0]])]});
            var Q1;
            Q1=makeQuery(id+"F16.imprint","IMPRINT",FACE,{"disambiguationData":[TD([[makeQuery(id+"F16.imprint","IMPRINT",EDGE,{"derivedFrom":sQuery(id+"F16.wireOp",EDGE,"E56.0")}),-1.0]])]});
            var Q2;
            Q2=makeQuery(id+"F16.imprint","IMPRINT",FACE,{"disambiguationData":[TD([[makeQuery(id+"F16.imprint","IMPRINT",EDGE,{"derivedFrom":sQuery(id+"F16.wireOp",EDGE,"E57")}),1.0]])]});
            extrude(context, id + "F18", {"entities" : qUnion([Q0, Q1, Q2]), "operationType" : NewBodyOperationType.REMOVE, "oppositeDirection" : true, "depth" : 25 * mm});
        }
    });
